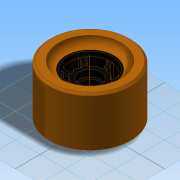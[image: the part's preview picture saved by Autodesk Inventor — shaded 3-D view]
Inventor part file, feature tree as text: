
AUTODESK INVENTOR PART (.ipt)
format: ipt  version: 2014 SP2 (Build 180246200, 246)  size: 388,096 bytes
history: native  units: in
note: dims shown in document units (in); Inventor stores cm internally (conversion verified against a paired STEP export)
features: extrude x4, chamfer x4, sketch x3, fillet x3, pattern_circular x2, revolve x1
ambient origin geometry x8: Origin, YZ Plane, XZ Plane, XY Plane, X Axis, Y Axis, Z Axis, Center Point
bodies: Solid1 (feature_tree)
feature tree (17):
  revolve  "Revolution1"  [1 undecoded]
  sketch  "Sketch3"  dims[d4=0.44in d6=0.815in]
  extrude  "Bearing Holder"  Depth=0.815in
  extrude  "Bearing Holder Lip"  Depth=0.01in
  extrude  "Spoke"  Depth=0.01in
  chamfer  "Chamfer1"  Distance=0.36in
  chamfer  "Chamfer2"  Angle=90.0deg  [1 undecoded]
  fillet  "Fillet1"  Radius=1.14in
  pattern_circular  "Spoke Pattern"  [2 undecoded]
  extrude  "Nib"  Depth=0.01in
  fillet  "Fillet2"  Radius=0.1in
  fillet  "Fillet3"  Radius=0.296in
  pattern_circular  "Nib Pattern"  [2 undecoded]
  chamfer  "Wheel Inner Chamfer"  Distance=0.296in
  chamfer  "Wheel Outer Chamfer"  Distance=0.168in Angle=45.0deg
  sketch  "Sketch2"  dims[d0=1.63in d2=0.38in]
  sketch  "Sketch5"  dims[d7=0.29in d9=1.025in d10=0.2898in d11=0.36in d12=90.0deg d13=1.14in d14=0.834in d15=0.0in d17=0.865in d18=0.1in d19=0.296in d20=0.0in d21=0.15in d22=0.296in d23=0.0in d24=0.168in d25=0.18in d26=45.0deg d27=0.05in d28=2.3622in d29=360.0deg d31=0.168in d32=0.18in d33=45.0deg d34=30.0deg d35=0.143in d36=0.04in d37=0.296in d38=0.0in d39=0.05in d40=0.01in d41=2.3622in d42=360.0deg d44=0.08in d45=0.18in d46=45.0deg d47=0.08in d48=0.292in d49=45.0deg]
note: 6 required parameter values undecoded (feature->parameter linkage not recoverable at this tier; creation-order binding heuristic only, values carry confidence <= 0.55)